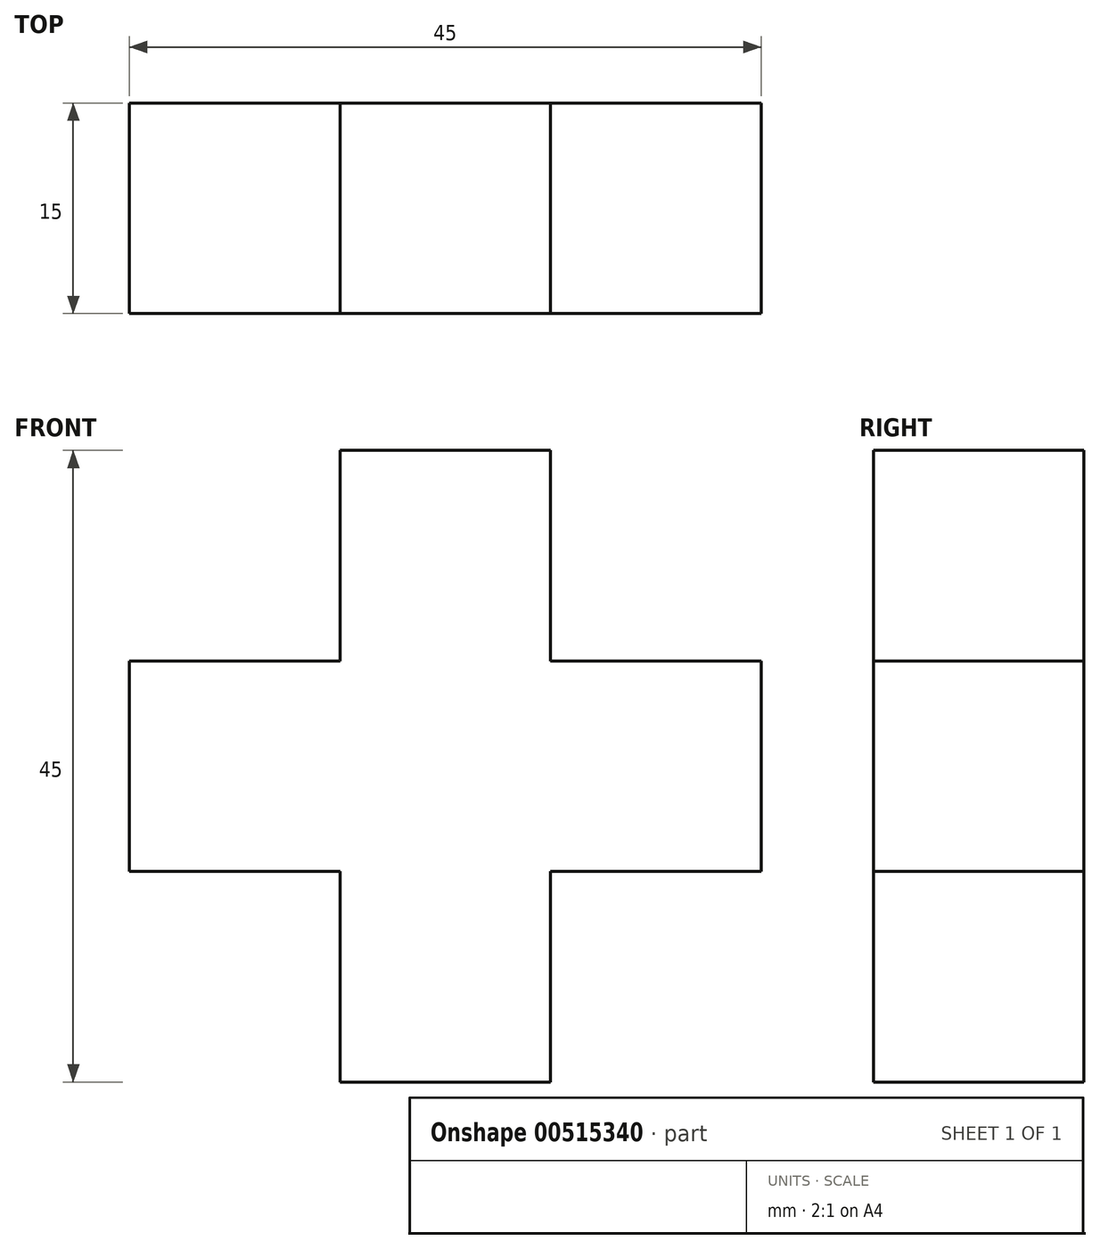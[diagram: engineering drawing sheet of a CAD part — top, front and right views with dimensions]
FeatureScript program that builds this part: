
annotation { "Feature Type Name" : "Feature", "Feature Type Description" : "" }
export const myFeature = defineFeature(function(context is Context, id is Id, definition is map)
    precondition{}
    {
        {
            var Q0;
            Q0=qCreatedBy(makeId("Front.planeOp"),FACE);
            var sketch = newSketch(context, id + "F0", { "sketchPlane" : qUnion([Q0])});
            skLineSegment(sketch, "E0.bottom", {"start": v(-30.7, 15.54) * mm, "end": v(-15.7, 15.54) * mm});
            skLineSegment(sketch, "E0.top", {"start": v(-30.7, -29.46) * mm, "end": v(-15.7, -29.46) * mm});
            skLineSegment(sketch, "E0.left", {"start": v(-30.7, 15.54) * mm, "end": v(-30.7, -29.46) * mm});
            skLineSegment(sketch, "E0.right", {"start": v(-15.7, 15.54) * mm, "end": v(-15.7, -29.46) * mm});
            skLineSegment(sketch, "E1.bottom", {"start": v(-45.7, 0.54) * mm, "end": v(-0.7, 0.54) * mm});
            skLineSegment(sketch, "E1.top", {"start": v(-45.7, -14.46) * mm, "end": v(-0.7, -14.46) * mm});
            skLineSegment(sketch, "E1.left", {"start": v(-45.7, 0.54) * mm, "end": v(-45.7, -14.46) * mm});
            skLineSegment(sketch, "E1.right", {"start": v(-0.7, 0.54) * mm, "end": v(-0.7, -14.46) * mm});
            skSolve(sketch);
        }
        {
            var Q0;
            Q0 = qSketchRegion(id + "F0", true);
            extrude(context, id + "F1", {"entities" : qUnion([Q0]), "depth" : 15 * mm, "offsetDistance" : 25 * mm});
        }
    });
